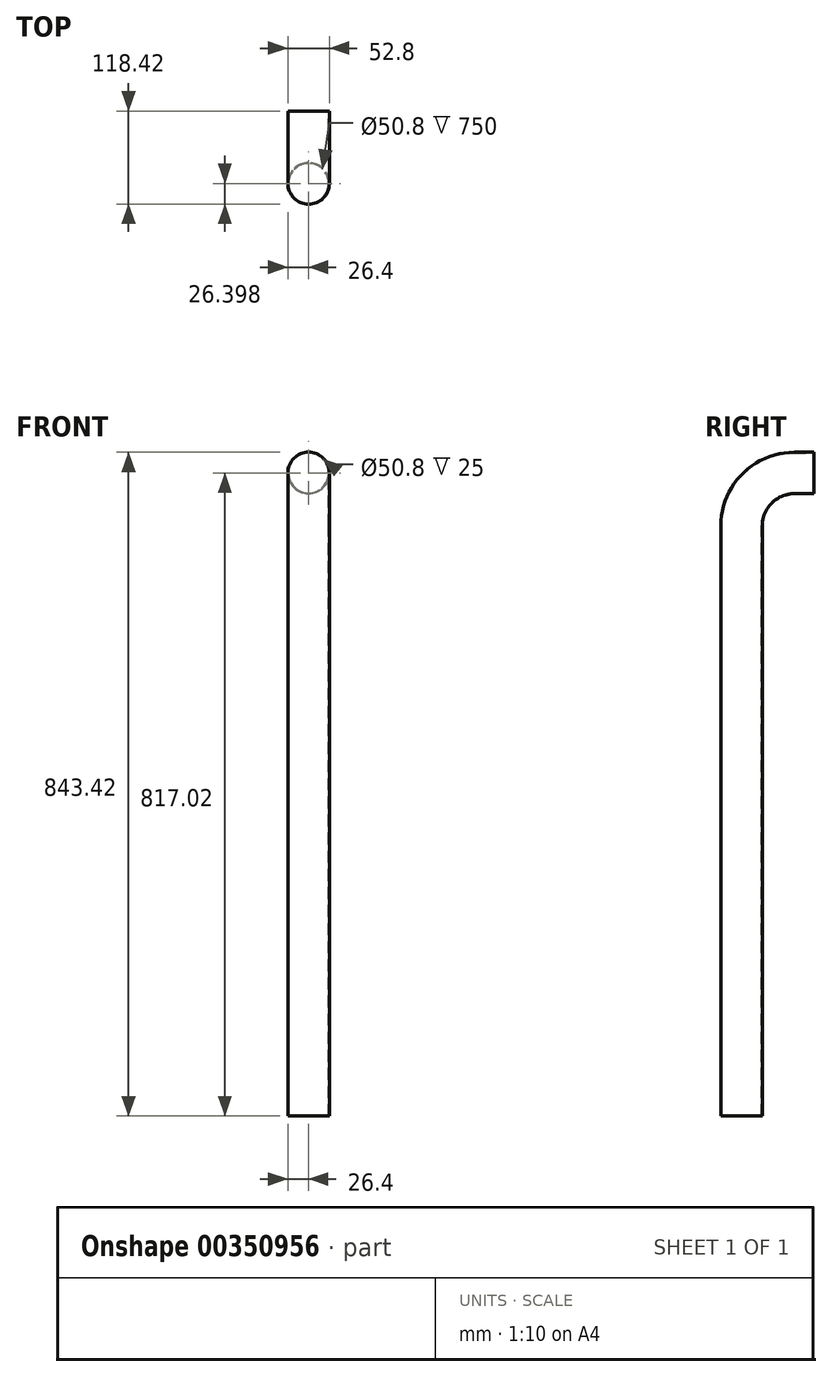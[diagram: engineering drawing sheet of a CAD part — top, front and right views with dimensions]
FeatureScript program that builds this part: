
annotation { "Feature Type Name" : "Feature", "Feature Type Description" : "" }
export const myFeature = defineFeature(function(context is Context, id is Id, definition is map)
    precondition{}
    {
        {
            var Q0;
            Q0=qCreatedBy(makeId("Front.planeOp"),FACE);
            var sketch = newSketch(context, id + "F0", { "sketchPlane" : qUnion([Q0])});
            skCircle(sketch, "E0", {"center": v(0, 0) * mm, "radius": 25.4 * mm});
            skCircle(sketch, "E1", {"center": v(0, 0) * mm, "radius": 26.4 * mm});
            skSolve(sketch);
        }
        {
            var Q0;
            Q0=makeQuery(id+"F0.imprint","IMPRINT",FACE,{"disambiguationData":[TD([[makeQuery(id+"F0.imprint","IMPRINT",EDGE,{"derivedFrom":sQuery(id+"F0.wireOp",EDGE,"E0")}),-1.0]])]});
            extrude(context, id + "F1", {"entities" : qUnion([Q0]), "depth" : 25 * mm});
        }
        {
            var Q0;
            Q0=qCreatedBy(makeId("Right.planeOp"),FACE);
            var sketch = newSketch(context, id + "F2", { "sketchPlane" : qUnion([Q0])});
            skLineSegment(sketch, "E2", {"start": v(0, 0) * mm, "end": v(-25, 0) * mm});
            skArc(sketch, "E3", {"start": v(-25, 0) * mm, "mid": v(-72.4, -19.63) * mm, "end": v(-92.02, -67.02) * mm});
            skLineSegment(sketch, "E4", {"start": v(-92.02, -67.02) * mm, "end": v(-92.02, 21.78) * mm});
            skSolve(sketch);
        }
        {
            var Q0;
            Q0=makeQuery(id+"F1.opExtrude","CAP_FACE",FACE,{"disambiguationData":[OSD([sQuery(id+"F0.wireOp",EDGE,"E0"),sQuery(id+"F0.wireOp",EDGE,"E1")])],"isStart":false});
            var Q1;
            Q1=sQuery(id+"F2.wireOp",EDGE,"E3");
            sweep(context, id + "F3", {"operationType" : NewBodyOperationType.ADD, "profiles" : qUnion([Q0]), "path" : qUnion([Q1])});
        }
        {
            var Q0;
            Q0=makeQuery(id+"F3.opSweep","CAP_FACE",FACE,{"disambiguationData":[OSD([sQuery(id+"F0.wireOp",EDGE,"E0"),sQuery(id+"F0.wireOp",EDGE,"E1"),sQuery(id+"F2.wireOp",VERTEX,"E3.end")])],"isStart":false});
            var sketch = newSketch(context, id + "F4", { "sketchPlane" : qUnion([Q0])});
            skSolve(sketch);
        }
        {
            var Q0;
            Q0 = qSketchRegion(id + "F4", true);
            var Q1;
            {var subQ0=sQuery(id+"F2.wireOp",VERTEX,"E3.end");Q1=makeQuery(id+"F4.imprint","IMPRINT",FACE,{"disambiguationData":[TD([[makeQuery(id+"F4.imprint","IMPRINT",EDGE,{"derivedFrom":makeQuery(id+"F3.opSweep","CAP_EDGE",EDGE,{"disambiguationData":[OSD([sQuery(id+"F0.wireOp",EDGE,"E0"),subQ0])],"isStart":false})}),-1.0]])]});}
            extrude(context, id + "F5", {"entities" : qUnion([Q0, Q1]), "operationType" : NewBodyOperationType.ADD, "depth" : 750 * mm});
        }
    });
